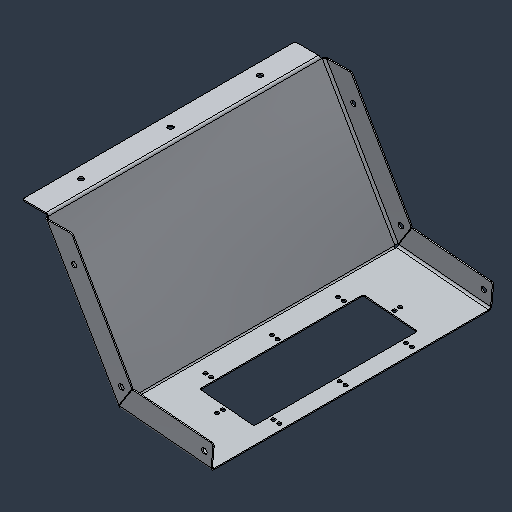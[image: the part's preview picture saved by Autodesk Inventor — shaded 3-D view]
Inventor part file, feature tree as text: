
AUTODESK INVENTOR PART (.ipt)
format: ipt  version: 2024.3 (Build 283343000, 343)  size: 198,144 bytes
history: native  units: mm (DEFAULTED — no unit token found)
features: fillet x1
ambient origin geometry x8: Origin, YZ Plane, XZ Plane, XY Plane, X Axis, Y Axis, Z Axis, Center Point
bodies: Solid1 (feature_tree)
feature tree (1):
  fillet  "Fillet5"  [1 undecoded]
note: 1 required parameter value undecoded (feature->parameter linkage not recoverable at this tier; creation-order binding heuristic only, values carry confidence <= 0.55)
